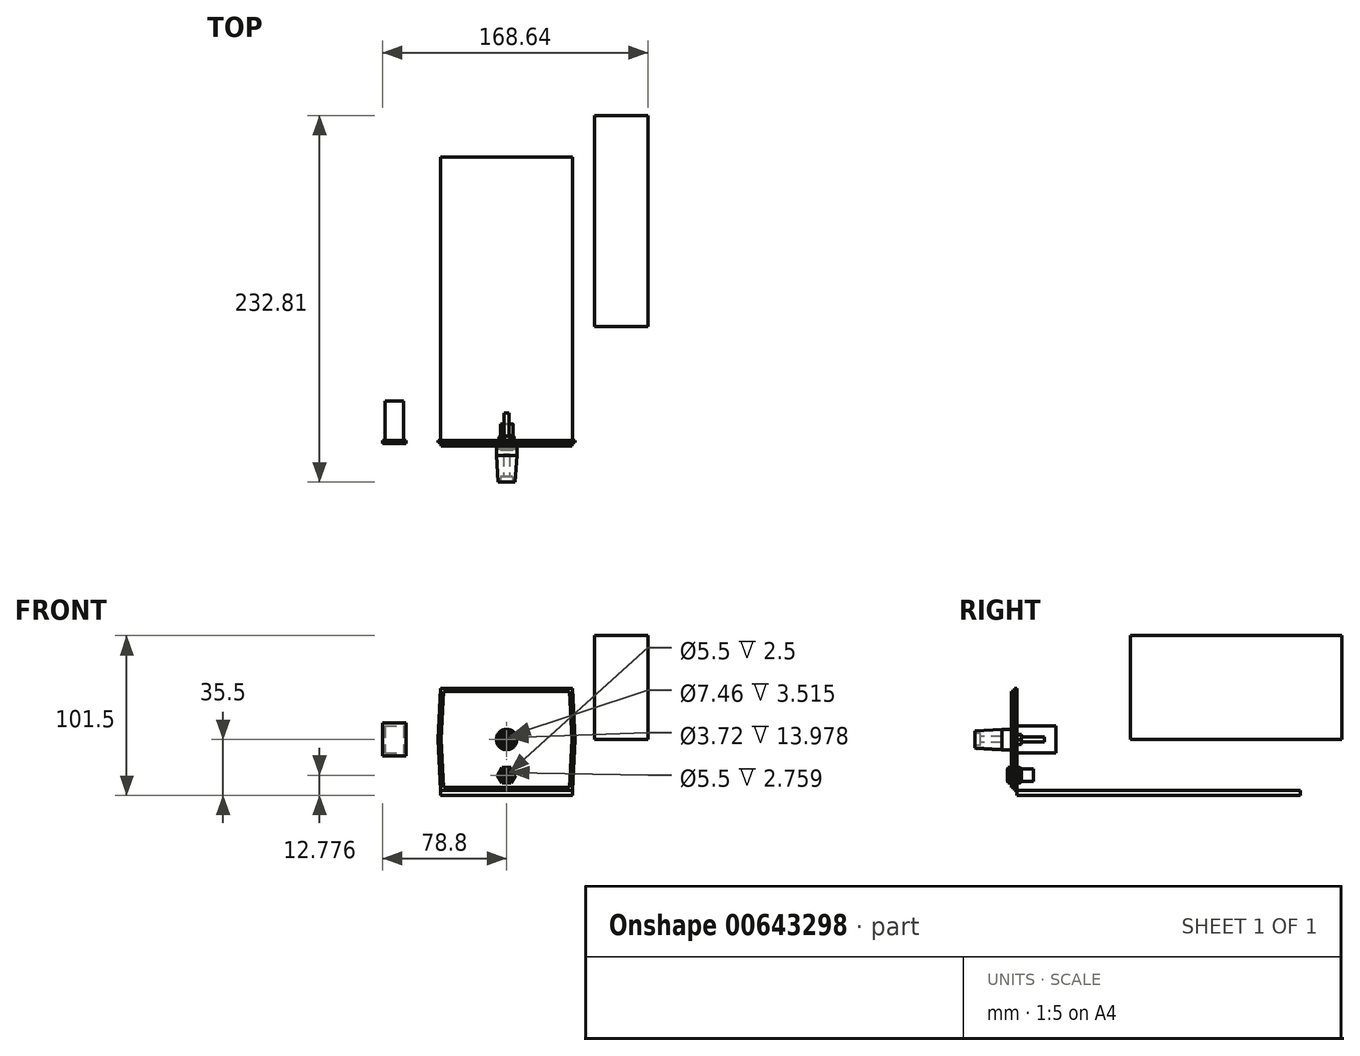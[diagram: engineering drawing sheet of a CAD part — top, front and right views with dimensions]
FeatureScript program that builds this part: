
annotation { "Feature Type Name" : "Feature", "Feature Type Description" : "" }
export const myFeature = defineFeature(function(context is Context, id is Id, definition is map)
    precondition{}
    {
        {
            var Q0;
            Q0=qCreatedBy(makeId("Front.planeOp"),FACE);
            var sketch = newSketch(context, id + "F0", { "sketchPlane" : qUnion([Q0])});
            skLineSegment(sketch, "E0.bottom", {"start": v(40, -30.5) * mm, "end": v(-40, -30.5) * mm});
            skLineSegment(sketch, "E0.top", {"start": v(40, 30.5) * mm, "end": v(-40, 30.5) * mm});
            skPoint(sketch, "E0.middle", {"position": v(0, 0) * mm});
            skLineSegment(sketch, "E1", {"start": v(-40, 30.5) * mm, "end": v(-41.5, 0) * mm});
            skLineSegment(sketch, "E2", {"start": v(-41.5, 0) * mm, "end": v(-40, -30.5) * mm});
            skLineSegment(sketch, "E3", {"start": v(40, 30.5) * mm, "end": v(41.5, 0) * mm});
            skLineSegment(sketch, "E4", {"start": v(41.5, 0) * mm, "end": v(40, -30.5) * mm});
            skPoint(sketch, "E5.endSnap0", {"position": v(0, -30.5) * mm});
            skLineSegment(sketch, "E6", {"start": v(0, 0) * mm, "end": v(41.5, 0) * mm, "construction": true});
            skLineSegment(sketch, "E7", {"start": v(0, 0) * mm, "end": v(-41.5, 0) * mm, "construction": true});
            skLineSegment(sketch, "E8.0", {"start": v(41.9, 32.5) * mm, "end": v(43.5, 0) * mm});
            skLineSegment(sketch, "E8.1", {"start": v(-41.9, 32.5) * mm, "end": v(-43.5, 0) * mm});
            skLineSegment(sketch, "E8.2", {"start": v(-43.5, 0) * mm, "end": v(-41.9, -32.5) * mm});
            skLineSegment(sketch, "E8.3", {"start": v(41.9, 32.5) * mm, "end": v(-41.9, 32.5) * mm});
            skLineSegment(sketch, "E8.4", {"start": v(41.9, -32.5) * mm, "end": v(-41.9, -32.5) * mm});
            skLineSegment(sketch, "E8.5", {"start": v(43.5, 0) * mm, "end": v(41.9, -32.5) * mm});
            skLineSegment(sketch, "E9.bottom", {"start": v(-77.3, 8.5) * mm, "end": v(-65.3, 8.5) * mm});
            skLineSegment(sketch, "E9.top", {"start": v(-77.3, -8.5) * mm, "end": v(-65.3, -8.5) * mm});
            skLineSegment(sketch, "E9.left", {"start": v(-77.3, 8.5) * mm, "end": v(-77.3, -8.5) * mm});
            skLineSegment(sketch, "E9.right", {"start": v(-65.3, 8.5) * mm, "end": v(-65.3, -8.5) * mm});
            skPoint(sketch, "E9.middle", {"position": v(-71.3, 0) * mm});
            skLineSegment(sketch, "E10.bottom", {"start": v(-63.8, -10.5) * mm, "end": v(-78.8, -10.5) * mm});
            skLineSegment(sketch, "E10.top", {"start": v(-63.8, 10.5) * mm, "end": v(-78.8, 10.5) * mm});
            skLineSegment(sketch, "E10.left", {"start": v(-63.8, -10.5) * mm, "end": v(-63.8, 10.5) * mm});
            skLineSegment(sketch, "E10.right", {"start": v(-78.8, -10.5) * mm, "end": v(-78.8, 10.5) * mm});
            skSolve(sketch);
        }
        {
            var Q0;
            Q0=makeQuery(id+"F0.imprint","IMPRINT",FACE,{"disambiguationData":[TD([[makeQuery(id+"F0.imprint","IMPRINT",EDGE,{"derivedFrom":sQuery(id+"F0.wireOp",EDGE,"E0.bottom")}),-1.0]])]});
            extrude(context, id + "F1", {"entities" : qUnion([Q0]), "depth" : 3.5 * mm, "offsetDistance" : 25 * mm});
        }
        {
            var Q0;
            Q0=makeQuery(id+"F0.imprint","IMPRINT",FACE,{"disambiguationData":[TD([[makeQuery(id+"F0.imprint","IMPRINT",EDGE,{"derivedFrom":sQuery(id+"F0.wireOp",EDGE,"E0.bottom")}),1.0]])]});
            extrude(context, id + "F2", {"entities" : qUnion([Q0]), "operationType" : NewBodyOperationType.ADD, "depth" : 1.5 * mm, "offsetDistance" : 25 * mm});
        }
        {
            var Q0;
            Q0=makeQuery(id+"F0.imprint","IMPRINT",FACE,{"disambiguationData":[TD([[makeQuery(id+"F0.imprint","IMPRINT",EDGE,{"derivedFrom":sQuery(id+"F0.wireOp",EDGE,"E9.bottom")}),-1.0]])]});
            extrude(context, id + "F3", {"entities" : qUnion([Q0]), "oppositeDirection" : true, "depth" : 25 * mm, "offsetDistance" : 25 * mm});
        }
        {
            var Q0;
            Q0=makeQuery(id+"F0.imprint","IMPRINT",FACE,{"disambiguationData":[TD([[makeQuery(id+"F0.imprint","IMPRINT",EDGE,{"derivedFrom":sQuery(id+"F0.wireOp",EDGE,"E9.bottom")}),1.0]])]});
            var Q1;
            Q1=makeQuery(id+"F0.imprint","IMPRINT",FACE,{"disambiguationData":[TD([[makeQuery(id+"F0.imprint","IMPRINT",EDGE,{"derivedFrom":sQuery(id+"F0.wireOp",EDGE,"E9.bottom")}),-1.0]])]});
            extrude(context, id + "F4", {"entities" : qUnion([Q0, Q1]), "operationType" : NewBodyOperationType.ADD, "depth" : 2 * mm, "offsetDistance" : 25 * mm});
        }
        {
            var Q0;
            Q0=qCreatedBy(makeId("Right.planeOp"),FACE);
            var sketch = newSketch(context, id + "F5", { "sketchPlane" : qUnion([Q0])});
            skLineSegment(sketch, "E11", {"start": v(-45.64, 0) * mm, "end": v(36.86, 0) * mm, "construction": true});
            skLineSegment(sketch, "E12.0", {"start": v(-3.5, 30.5) * mm, "end": v(-3.5, 0) * mm});
            skLineSegment(sketch, "E13", {"start": v(-26.5, 5.5) * mm, "end": v(-26.5, 0) * mm});
            skLineSegment(sketch, "E14", {"start": v(-26.5, 0) * mm, "end": v(-3.5, 0) * mm});
            skLineSegment(sketch, "E15", {"start": v(-9.5, 6.5) * mm, "end": v(-26.5, 5.5) * mm});
            skLineSegment(sketch, "E16", {"start": v(-9.5, 6.5) * mm, "end": v(-3.5, 6.5) * mm});
            skLineSegment(sketch, "E17", {"start": v(-3.5, 3.25) * mm, "end": v(-0.5, 3.25) * mm});
            skLineSegment(sketch, "E18", {"start": v(-0.5, 3.25) * mm, "end": v(-0.5, 0) * mm});
            skLineSegment(sketch, "E19", {"start": v(-0.5, 1.5) * mm, "end": v(17.5, 1.5) * mm});
            skLineSegment(sketch, "E20", {"start": v(17.5, 1.5) * mm, "end": v(17.5, 0) * mm});
            skLineSegment(sketch, "E21", {"start": v(17.5, 0) * mm, "end": v(-3.5, 0) * mm});
            skLineSegment(sketch, "E22", {"start": v(-26.5, 3.73) * mm, "end": v(-22.98, 3.73) * mm});
            skLineSegment(sketch, "E23", {"start": v(-22.98, 3.73) * mm, "end": v(-22.98, 1.86) * mm});
            skLineSegment(sketch, "E24", {"start": v(-22.98, 1.86) * mm, "end": v(-9, 1.86) * mm});
            skLineSegment(sketch, "E25", {"start": v(-9, 1.86) * mm, "end": v(-9, 0) * mm});
            skLineSegment(sketch, "E26.0", {"start": v(0, 0) * mm, "end": v(0, -32.5) * mm});
            skLineSegment(sketch, "E27", {"start": v(-11.5, -22.72) * mm, "end": v(18.32, -22.72) * mm, "construction": true});
            skLineSegment(sketch, "E28", {"start": v(0, -17.88) * mm, "end": v(2.15, -17.88) * mm});
            skLineSegment(sketch, "E29", {"start": v(2.15, -17.88) * mm, "end": v(3, -18.74) * mm});
            skLineSegment(sketch, "E30", {"start": v(3, -18.74) * mm, "end": v(10.5, -18.74) * mm});
            skLineSegment(sketch, "E31", {"start": v(10.5, -18.74) * mm, "end": v(10.5, -22.72) * mm});
            skLineSegment(sketch, "E32", {"start": v(0, -18.72) * mm, "end": v(-6, -18.72) * mm});
            skLineSegment(sketch, "E33", {"start": v(-6, -18.72) * mm, "end": v(-6, -22.72) * mm});
            skLineSegment(sketch, "E34", {"start": v(-6, -22.72) * mm, "end": v(10.5, -22.72) * mm});
            skLineSegment(sketch, "E35", {"start": v(-6, -19.97) * mm, "end": v(2.76, -19.97) * mm});
            skLineSegment(sketch, "E36", {"start": v(2.76, -19.97) * mm, "end": v(2.76, -22.72) * mm});
            skLineSegment(sketch, "E37", {"start": v(2.76, -21.67) * mm, "end": v(-4.18, -21.67) * mm});
            skLineSegment(sketch, "E38", {"start": v(-4.18, -21.67) * mm, "end": v(-4.18, -22.72) * mm});
            skSolve(sketch);
        }
        {
            var Q0;
            {var subQ0=sQuery(id+"F5.wireOp",EDGE,"E15");Q0=makeQuery(id+"F5.imprint","IMPRINT",FACE,{"disambiguationData":[TD([[makeQuery(id+"F5.imprint","IMPRINT",EDGE,{"derivedFrom":subQ0}),1.0]])]});}
            var Q1;
            {var subQ4=sQuery(id+"F5.wireOp",EDGE,"E17");Q1=makeQuery(id+"F5.imprint","IMPRINT",FACE,{"disambiguationData":[TD([[makeQuery(id+"F5.imprint","IMPRINT",EDGE,{"derivedFrom":subQ4}),-1.0]])]});}
            var Q2;
            {var subQ3=sQuery(id+"F5.wireOp",EDGE,"E19");Q2=makeQuery(id+"F5.imprint","IMPRINT",FACE,{"disambiguationData":[TD([[makeQuery(id+"F5.imprint","IMPRINT",EDGE,{"derivedFrom":subQ3}),-1.0]])]});}
            var Q3;
            Q3=sQuery(id+"F5.wireOp",EDGE,"E14");
            revolve(context, id + "F6", {"entities" : qUnion([Q0, Q1, Q2]), "axis" : qUnion([Q3]), "revolveType" : RevolveType.FULL});
        }
        {
            var Q0;
            {var subQ5=sQuery(id+"F5.wireOp",EDGE,"E38");Q0=makeQuery(id+"F5.imprint","IMPRINT",FACE,{"disambiguationData":[TD([[makeQuery(id+"F5.imprint","IMPRINT",EDGE,{"derivedFrom":subQ5}),1.0]])]});}
            var Q1;
            {var subQ0=sQuery(id+"F5.wireOp",EDGE,"E34");var subQ1=sQuery(id+"F5.wireOp",EDGE,"E26.0");var subQ2=makeQuery(id+"F5.imprint","INTERSECT",VERTEX,{"derivedFrom":[subQ1,subQ0]});Q1=makeQuery(id+"F5.imprint","IMPRINT",FACE,{"disambiguationData":[TD([[makeQuery(id+"F5.imprint","IMPRINT",EDGE,{"disambiguationData":[TD([[subQ2,1.0]])],"derivedFrom":subQ1}),1.0]])]});}
            var Q2;
            {var subQ0=sQuery(id+"F5.wireOp",EDGE,"E28");Q2=makeQuery(id+"F5.imprint","IMPRINT",FACE,{"disambiguationData":[TD([[makeQuery(id+"F5.imprint","IMPRINT",EDGE,{"derivedFrom":subQ0}),-1.0]])]});}
            var Q3;
            {var subQ0=sQuery(id+"F5.wireOp",EDGE,"E32");Q3=makeQuery(id+"F5.imprint","IMPRINT",FACE,{"disambiguationData":[TD([[makeQuery(id+"F5.imprint","IMPRINT",EDGE,{"derivedFrom":subQ0}),1.0]])]});}
            var Q4;
            Q4=sQuery(id+"F5.wireOp",EDGE,"E27");
            revolve(context, id + "F7", {"entities" : qUnion([Q0, Q1, Q2, Q3]), "axis" : qUnion([Q4]), "revolveType" : RevolveType.FULL});
        }
        {
            var Q0;
            Q0=makeQuery(id+"F1.opExtrude","CAP_FACE",FACE,{"disambiguationData":[OSD([sQuery(id+"F0.wireOp",EDGE,"E0.bottom"),sQuery(id+"F0.wireOp",EDGE,"E0.top"),sQuery(id+"F0.wireOp",EDGE,"E1"),sQuery(id+"F0.wireOp",EDGE,"E2"),sQuery(id+"F0.wireOp",EDGE,"E3"),sQuery(id+"F0.wireOp",EDGE,"E4")])],"isStart":false});
            var sketch = newSketch(context, id + "F8", { "sketchPlane" : qUnion([Q0])});
            skPoint(sketch, "E39.0", {"position": v(0, -22.72) * mm});
            skCircle(sketch, "E40.cCircle", {"center": v(0, -22.72) * mm, "radius": 5 * mm, "construction": true});
            skLineSegment(sketch, "E40.0", {"start": v(2.9, -17.73) * mm, "end": v(5.77, -22.74) * mm});
            skLineSegment(sketch, "E40.1", {"start": v(5.77, -22.74) * mm, "end": v(2.87, -27.73) * mm});
            skLineSegment(sketch, "E40.2", {"start": v(2.87, -27.73) * mm, "end": v(-2.9, -27.72) * mm});
            skLineSegment(sketch, "E40.3", {"start": v(-2.9, -27.72) * mm, "end": v(-5.77, -22.7) * mm});
            skLineSegment(sketch, "E40.4", {"start": v(-5.77, -22.7) * mm, "end": v(-2.87, -17.72) * mm});
            skLineSegment(sketch, "E40.5", {"start": v(-2.87, -17.72) * mm, "end": v(2.9, -17.73) * mm});
            skPoint(sketch, "E40.0.midPoint", {"position": v(4.34, -20.24) * mm});
            skCircle(sketch, "E41.0", {"center": v(0, -22.72) * mm, "radius": 4 * mm});
            skSolve(sketch);
        }
        {
            var Q0;
            Q0 = qSketchRegion(id + "F8", true);
            extrude(context, id + "F9", {"entities" : qUnion([Q0]), "operationType" : NewBodyOperationType.ADD, "depth" : 2 * mm, "offsetDistance" : 25 * mm});
        }
        {
            var Q0;
            Q0=makeQuery(id+"F0.imprint","IMPRINT",FACE,{"disambiguationData":[TD([[makeQuery(id+"F0.imprint","IMPRINT",EDGE,{"derivedFrom":sQuery(id+"F0.wireOp",EDGE,"E0.bottom")}),-1.0]])]});
            var sketch = newSketch(context, id + "F10", { "sketchPlane" : qUnion([Q0])});
            skCircle(sketch, "E42.cCircle", {"center": v(0, 0) * mm, "radius": 3 * mm, "construction": true});
            skLineSegment(sketch, "E42.0", {"start": v(-3.45, 0.36) * mm, "end": v(-1.41, 3.16) * mm});
            skLineSegment(sketch, "E42.1", {"start": v(-1.41, 3.16) * mm, "end": v(2.03, 2.8) * mm});
            skLineSegment(sketch, "E42.2", {"start": v(2.03, 2.8) * mm, "end": v(3.45, -0.36) * mm});
            skLineSegment(sketch, "E42.3", {"start": v(3.45, -0.36) * mm, "end": v(1.41, -3.16) * mm});
            skLineSegment(sketch, "E42.4", {"start": v(1.41, -3.16) * mm, "end": v(-2.03, -2.8) * mm});
            skLineSegment(sketch, "E42.5", {"start": v(-2.03, -2.8) * mm, "end": v(-3.45, 0.36) * mm});
            skPoint(sketch, "E42.0.midPoint", {"position": v(-2.43, 1.76) * mm});
            skSolve(sketch);
        }
        {
            var Q0;
            Q0 = qSketchRegion(id + "F10", true);
            extrude(context, id + "F11", {"entities" : qUnion([Q0]), "operationType" : NewBodyOperationType.ADD, "oppositeDirection" : true, "depth" : 2.8 * mm, "offsetDistance" : 25 * mm});
        }
        {
            var Q0;
            Q0=qCreatedBy(makeId("Top.planeOp"),FACE);
            var sketch = newSketch(context, id + "F12", { "sketchPlane" : qUnion([Q0])});
            skLineSegment(sketch, "E43.bottom", {"start": v(55.84, 72.3) * mm, "end": v(89.84, 72.3) * mm});
            skLineSegment(sketch, "E43.top", {"start": v(55.84, 206.3) * mm, "end": v(89.84, 206.3) * mm});
            skLineSegment(sketch, "E43.left", {"start": v(55.84, 72.3) * mm, "end": v(55.84, 206.3) * mm});
            skLineSegment(sketch, "E43.right", {"start": v(89.84, 72.3) * mm, "end": v(89.84, 206.3) * mm});
            skSolve(sketch);
        }
        {
            var Q0;
            Q0 = qSketchRegion(id + "F12", true);
            extrude(context, id + "F13", {"entities" : qUnion([Q0]), "depth" : 66 * mm, "offsetDistance" : 25 * mm});
        }
        {
            var Q0;
            Q0=qCreatedBy(makeId("Front.planeOp"),FACE);
            var sketch = newSketch(context, id + "F14", { "sketchPlane" : qUnion([Q0])});
            skLineSegment(sketch, "E44.0", {"start": v(41.9, -32.5) * mm, "end": v(-41.9, -32.5) * mm});
            skLineSegment(sketch, "E45.0", {"start": v(41.9, -35.5) * mm, "end": v(-41.9, -35.5) * mm});
            skLineSegment(sketch, "E46", {"start": v(41.9, -32.5) * mm, "end": v(41.9, -35.5) * mm});
            skLineSegment(sketch, "E47", {"start": v(-41.9, -32.5) * mm, "end": v(-41.9, -35.5) * mm});
            skSolve(sketch);
        }
        {
            var Q0;
            Q0=makeQuery(id+"F14.imprint","IMPRINT",FACE,{"disambiguationData":[TD([[makeQuery(id+"F14.imprint","IMPRINT",EDGE,{"derivedFrom":sQuery(id+"F14.wireOp",EDGE,"E44.0")}),1.0]])]});
            extrude(context, id + "F15", {"entities" : qUnion([Q0]), "oppositeDirection" : true, "depth" : 180 * mm, "offsetDistance" : 25 * mm});
        }
    });
